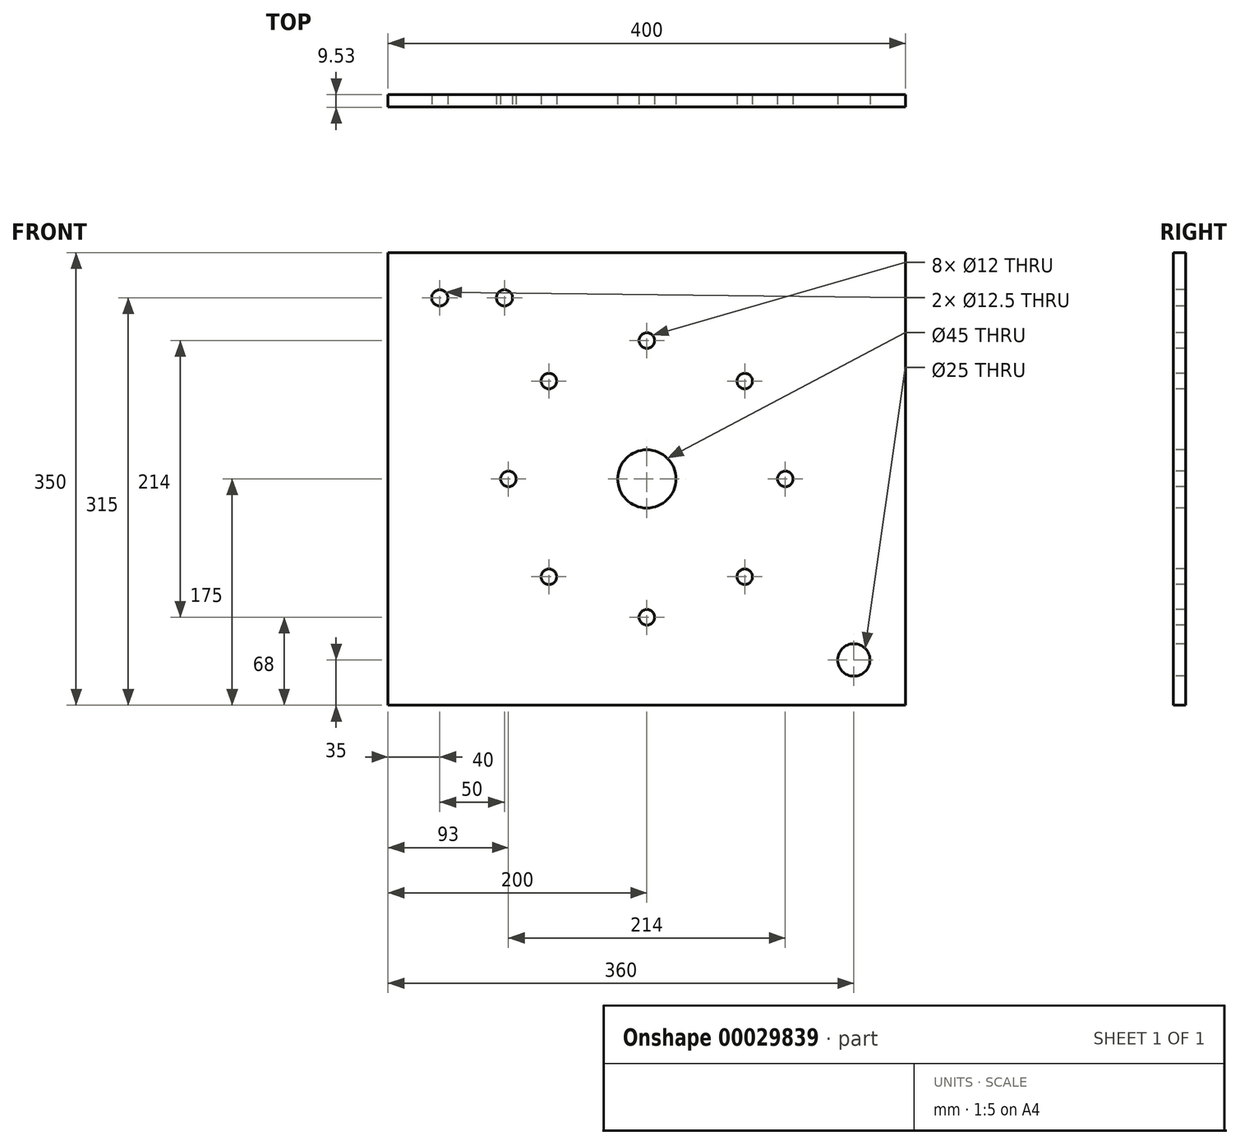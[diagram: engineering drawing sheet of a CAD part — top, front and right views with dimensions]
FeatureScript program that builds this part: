
annotation { "Feature Type Name" : "Feature", "Feature Type Description" : "" }
export const myFeature = defineFeature(function(context is Context, id is Id, definition is map)
    precondition{}
    {
        {
            var Q0;
            Q0=qCreatedBy(makeId("Front.planeOp"),FACE);
            var sketch = newSketch(context, id + "F3", { "sketchPlane" : qUnion([Q0])});
            skLineSegment(sketch, "E0.rect.bottom", {"start": v(-200, 175) * mm, "end": v(200, 175) * mm});
            skLineSegment(sketch, "E0.rect.top", {"start": v(-200, -175) * mm, "end": v(200, -175) * mm});
            skLineSegment(sketch, "E0.rect.left", {"start": v(-200, 175) * mm, "end": v(-200, -175) * mm});
            skLineSegment(sketch, "E0.rect.right", {"start": v(200, 175) * mm, "end": v(200, -175) * mm});
            skPoint(sketch, "E0.rect.middle", {"position": v(0, 0) * mm});
            skSolve(sketch);
        }
        {
            var Q0;
            Q0=qSketchRegion(id+"F3",true);
            extrude(context, id + "F4", {"entities" : qUnion([Q0]), "depth" : 9.52 * mm});
        }
        {
            var Q0;
            Q0=makeQuery(id+"F4.opExtrude","CAP_FACE",FACE,{"disambiguationData":[OSD([sQuery(id+"F3.wireOp",EDGE,"E0.rect.bottom"),sQuery(id+"F3.wireOp",EDGE,"E0.rect.top"),sQuery(id+"F3.wireOp",EDGE,"E0.rect.left"),sQuery(id+"F3.wireOp",EDGE,"E0.rect.right")])],"isStart":false});
            var sketch = newSketch(context, id + "F5", { "sketchPlane" : qUnion([Q0])});
            skCircle(sketch, "E1", {"center": v(0, 107) * mm, "radius": 6 * mm});
            skCircle(sketch, "E2", {"center": v(0, 0) * mm, "radius": 107 * mm, "construction": true});
            skCircle(sketch, "E3", {"center": v(75.66, 75.66) * mm, "radius": 6 * mm});
            skCircle(sketch, "E4", {"center": v(107, 0) * mm, "radius": 6 * mm});
            skLineSegment(sketch, "E5", {"start": v(75.66, 75.66) * mm, "end": v(0, 0) * mm, "construction": true});
            skLineSegment(sketch, "E6", {"start": v(0, 107) * mm, "end": v(0, 0) * mm, "construction": true});
            skLineSegment(sketch, "E7", {"start": v(0, 0) * mm, "end": v(-75.66, -75.66) * mm});
            skLineSegment(sketch, "E8", {"start": v(-75.66, 75.66) * mm, "end": v(0, 0) * mm});
            skLineSegment(sketch, "E9", {"start": v(75.66, -75.66) * mm, "end": v(0, 0) * mm});
            skCircle(sketch, "E10", {"center": v(75.66, -75.66) * mm, "radius": 6 * mm});
            skCircle(sketch, "E11", {"center": v(0, -107) * mm, "radius": 6 * mm});
            skCircle(sketch, "E12", {"center": v(-75.66, -75.66) * mm, "radius": 6 * mm});
            skCircle(sketch, "E13", {"center": v(-107, 0) * mm, "radius": 6 * mm});
            skCircle(sketch, "E14", {"center": v(-75.66, 75.66) * mm, "radius": 6 * mm});
            skCircle(sketch, "E15", {"center": v(0, 0) * mm, "radius": 22.5 * mm});
            skSolve(sketch);
        }
        {
            var Q0;
            Q0=qSketchRegion(id+"F5",true);
            extrude(context, id + "F0", {"entities" : qUnion([Q0]), "operationType" : NewBodyOperationType.REMOVE, "endBound" : BoundingType.UP_TO_NEXT, "oppositeDirection" : true, "depth" : 25 * mm});
        }
        {
            var Q0;
            Q0=makeQuery(id+"F4.opExtrude","CAP_FACE",FACE,{"disambiguationData":[OSD([sQuery(id+"F3.wireOp",EDGE,"E0.rect.bottom"),sQuery(id+"F3.wireOp",EDGE,"E0.rect.top"),sQuery(id+"F3.wireOp",EDGE,"E0.rect.left"),sQuery(id+"F3.wireOp",EDGE,"E0.rect.right")])],"isStart":false});
            var sketch = newSketch(context, id + "F1", { "sketchPlane" : qUnion([Q0])});
            skCircle(sketch, "E16", {"center": v(-110, 140) * mm, "radius": 6.25 * mm});
            skCircle(sketch, "E17", {"center": v(-160, 140) * mm, "radius": 6.25 * mm});
            skCircle(sketch, "E18", {"center": v(160, -140) * mm, "radius": 12.5 * mm});
            skSolve(sketch);
        }
        {
            var Q0;
            Q0=qSketchRegion(id+"F1",true);
            extrude(context, id + "F2", {"entities" : qUnion([Q0]), "operationType" : NewBodyOperationType.REMOVE, "endBound" : BoundingType.UP_TO_NEXT, "oppositeDirection" : true, "depth" : 25 * mm});
        }
    });
